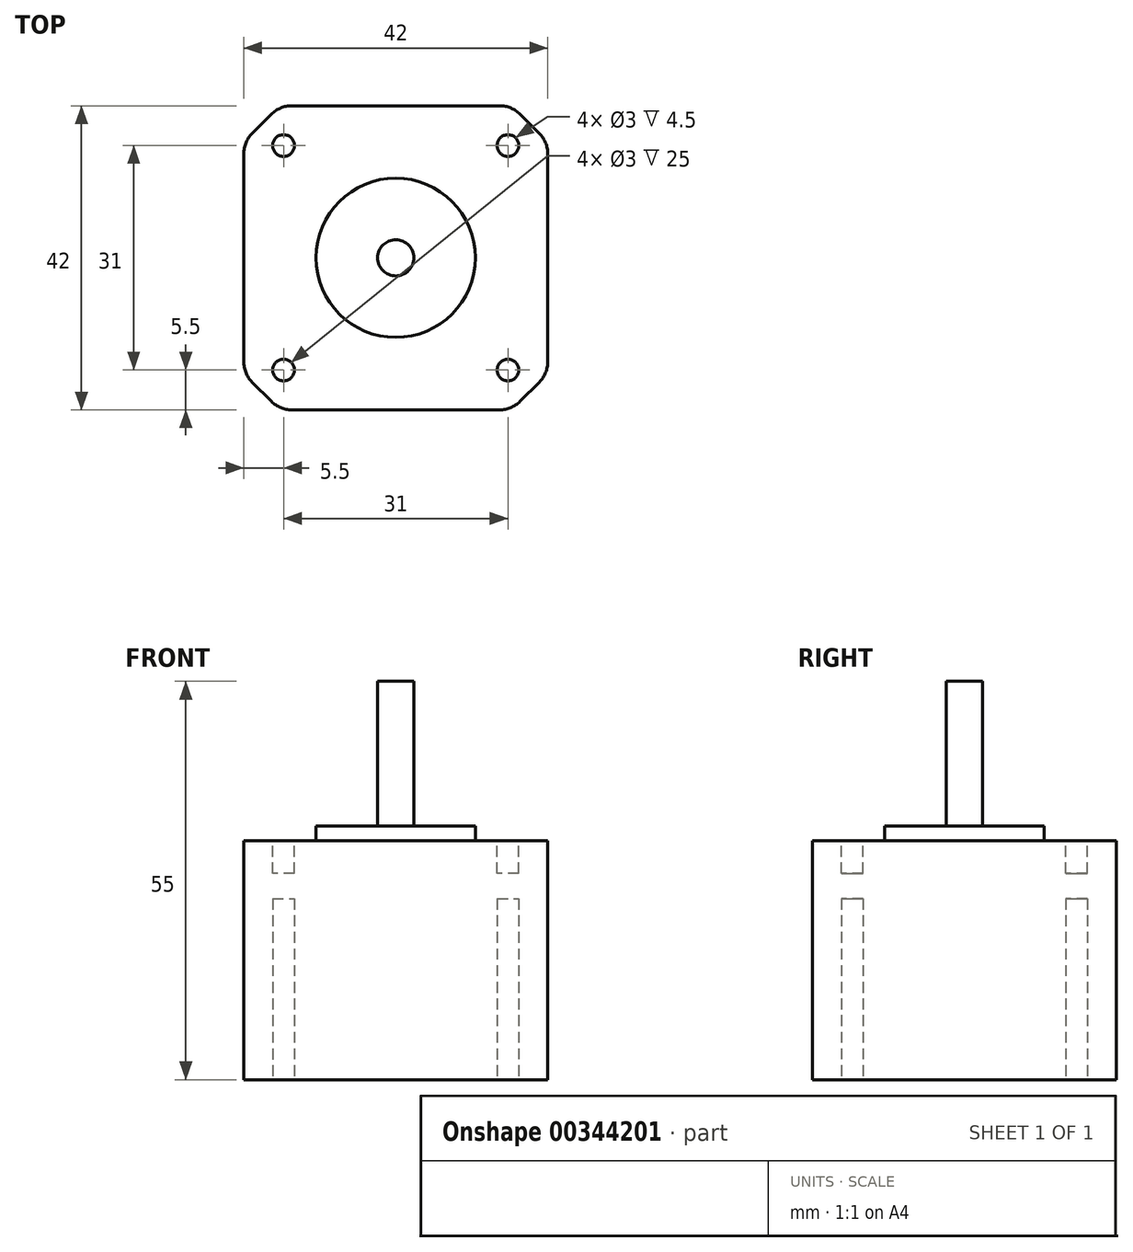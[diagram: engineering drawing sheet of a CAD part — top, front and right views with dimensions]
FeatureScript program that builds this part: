
annotation { "Feature Type Name" : "Feature", "Feature Type Description" : "" }
export const myFeature = defineFeature(function(context is Context, id is Id, definition is map)
    precondition{}
    {
        {
            var Q0;
            Q0=qCreatedBy(makeId("Top.planeOp"),FACE);
            var sketch = newSketch(context, id + "F0", { "sketchPlane" : qUnion([Q0])});
            skLineSegment(sketch, "E0.bottom", {"start": v(0, 0) * mm, "end": v(42, 0) * mm});
            skLineSegment(sketch, "E0.top", {"start": v(0, -42) * mm, "end": v(42, -42) * mm});
            skLineSegment(sketch, "E0.left", {"start": v(0, 0) * mm, "end": v(0, -42) * mm});
            skLineSegment(sketch, "E0.right", {"start": v(42, 0) * mm, "end": v(42, -42) * mm});
            skSolve(sketch);
        }
        {
            var Q0;
            Q0 = qSketchRegion(id + "F0", true);
            extrude(context, id + "F1", {"entities" : qUnion([Q0]), "depth" : 33 * mm});
        }
        {
            var Q0;
            Q0=makeQuery(id+"F1.opExtrude","CAP_FACE",FACE,{"disambiguationData":[OSD([sQuery(id+"F0.wireOp",EDGE,"E0.bottom"),sQuery(id+"F0.wireOp",EDGE,"E0.top"),sQuery(id+"F0.wireOp",EDGE,"E0.left"),sQuery(id+"F0.wireOp",EDGE,"E0.right")])],"isStart":false});
            var sketch = newSketch(context, id + "F2", { "sketchPlane" : qUnion([Q0])});
            skCircle(sketch, "E1", {"center": v(21, -21) * mm, "radius": 11 * mm});
            skPoint(sketch, "E1.centerSnap0", {"position": v(21, 0) * mm});
            skPoint(sketch, "E1.centerSnap1", {"position": v(42, -21) * mm});
            skSolve(sketch);
        }
        {
            var Q0;
            Q0 = qSketchRegion(id + "F2", true);
            extrude(context, id + "F3", {"entities" : qUnion([Q0]), "operationType" : NewBodyOperationType.ADD, "depth" : 2 * mm});
        }
        {
            var Q0;
            Q0=makeQuery(id+"F3.opExtrude","CAP_FACE",FACE,{"disambiguationData":[OSD([sQuery(id+"F2.wireOp",EDGE,"E1")])],"isStart":false});
            var sketch = newSketch(context, id + "F4", { "sketchPlane" : qUnion([Q0])});
            skCircle(sketch, "E2", {"center": v(21, -21) * mm, "radius": 2.5 * mm});
            skSolve(sketch);
        }
        {
            var Q0;
            Q0 = qSketchRegion(id + "F4", true);
            extrude(context, id + "F5", {"entities" : qUnion([Q0]), "operationType" : NewBodyOperationType.ADD, "depth" : 20 * mm});
        }
        {
            var Q0;
            Q0=makeQuery(id+"F1.opExtrude","CAP_FACE",FACE,{"disambiguationData":[OSD([sQuery(id+"F0.wireOp",EDGE,"E0.bottom"),sQuery(id+"F0.wireOp",EDGE,"E0.top"),sQuery(id+"F0.wireOp",EDGE,"E0.left"),sQuery(id+"F0.wireOp",EDGE,"E0.right")])],"isStart":false});
            var sketch = newSketch(context, id + "F6", { "sketchPlane" : qUnion([Q0])});
            skCircle(sketch, "E3", {"center": v(5.5, -5.5) * mm, "radius": 1.5 * mm});
            skCircle(sketch, "E4", {"center": v(36.5, -5.5) * mm, "radius": 1.5 * mm});
            skCircle(sketch, "E5", {"center": v(36.5, -36.5) * mm, "radius": 1.5 * mm});
            skCircle(sketch, "E6", {"center": v(5.5, -36.5) * mm, "radius": 1.5 * mm});
            skSolve(sketch);
        }
        {
            var Q0;
            Q0 = qSketchRegion(id + "F6", true);
            extrude(context, id + "F7", {"entities" : qUnion([Q0]), "operationType" : NewBodyOperationType.REMOVE, "oppositeDirection" : true, "depth" : 4.5 * mm});
        }
        {
            var Q0;
            Q0=makeQuery(id+"F1.opExtrude","SWEPT_EDGE",EDGE,{"disambiguationData":[OSD([sQuery(id+"F0.wireOp",EDGE,"E0.bottom"),sQuery(id+"F0.wireOp",EDGE,"E0.right")])]});
            var Q1;
            Q1=makeQuery(id+"F1.opExtrude","SWEPT_EDGE",EDGE,{"disambiguationData":[OSD([sQuery(id+"F0.wireOp",EDGE,"E0.top"),sQuery(id+"F0.wireOp",EDGE,"E0.right")])]});
            var Q2;
            Q2=makeQuery(id+"F1.opExtrude","SWEPT_EDGE",EDGE,{"disambiguationData":[OSD([sQuery(id+"F0.wireOp",EDGE,"E0.top"),sQuery(id+"F0.wireOp",EDGE,"E0.left")])]});
            var Q3;
            Q3=makeQuery(id+"F1.opExtrude","SWEPT_EDGE",EDGE,{"disambiguationData":[OSD([sQuery(id+"F0.wireOp",EDGE,"E0.bottom"),sQuery(id+"F0.wireOp",EDGE,"E0.left")])]});
            chamfer(context, id + "F8", {"entities" : qUnion([Q0, Q1, Q2, Q3]), "width" : 5 * mm, "tangentPropagation" : true});
        }
        {
            var Q0;
            {var subQ0=sQuery(id+"F0.wireOp",EDGE,"E0.left");Q0=makeQuery(id+"F8.opChamfer","BLEND_EDGE",EDGE,{"blendedFrom":[makeQuery(id+"F1.opExtrude","SWEPT_EDGE",EDGE,{"disambiguationData":[OSD([sQuery(id+"F0.wireOp",EDGE,"E0.bottom"),subQ0])]}),makeQuery(id+"F1.opExtrude","SWEPT_FACE",FACE,{"disambiguationData":[OSD([subQ0])]})],"blendedInto":[makeQuery(id+"F1.opExtrude","SWEPT_FACE",FACE,{"disambiguationData":[OSD([subQ0])]})]});}
            var Q1;
            {var subQ0=sQuery(id+"F0.wireOp",EDGE,"E0.bottom");Q1=makeQuery(id+"F8.opChamfer","BLEND_EDGE",EDGE,{"blendedFrom":[makeQuery(id+"F1.opExtrude","SWEPT_EDGE",EDGE,{"disambiguationData":[OSD([subQ0,sQuery(id+"F0.wireOp",EDGE,"E0.left")])]}),makeQuery(id+"F1.opExtrude","SWEPT_FACE",FACE,{"disambiguationData":[OSD([subQ0])]})],"blendedInto":[makeQuery(id+"F1.opExtrude","SWEPT_FACE",FACE,{"disambiguationData":[OSD([subQ0])]})]});}
            var Q2;
            {var subQ0=sQuery(id+"F0.wireOp",EDGE,"E0.left");Q2=makeQuery(id+"F8.opChamfer","BLEND_EDGE",EDGE,{"blendedFrom":[makeQuery(id+"F1.opExtrude","SWEPT_EDGE",EDGE,{"disambiguationData":[OSD([sQuery(id+"F0.wireOp",EDGE,"E0.top"),subQ0])]}),makeQuery(id+"F1.opExtrude","SWEPT_FACE",FACE,{"disambiguationData":[OSD([subQ0])]})],"blendedInto":[makeQuery(id+"F1.opExtrude","SWEPT_FACE",FACE,{"disambiguationData":[OSD([subQ0])]})]});}
            var Q3;
            {var subQ0=sQuery(id+"F0.wireOp",EDGE,"E0.top");Q3=makeQuery(id+"F8.opChamfer","BLEND_EDGE",EDGE,{"blendedFrom":[makeQuery(id+"F1.opExtrude","SWEPT_EDGE",EDGE,{"disambiguationData":[OSD([subQ0,sQuery(id+"F0.wireOp",EDGE,"E0.left")])]}),makeQuery(id+"F1.opExtrude","SWEPT_FACE",FACE,{"disambiguationData":[OSD([subQ0])]})],"blendedInto":[makeQuery(id+"F1.opExtrude","SWEPT_FACE",FACE,{"disambiguationData":[OSD([subQ0])]})]});}
            var Q4;
            {var subQ0=sQuery(id+"F0.wireOp",EDGE,"E0.top");Q4=makeQuery(id+"F8.opChamfer","BLEND_EDGE",EDGE,{"blendedFrom":[makeQuery(id+"F1.opExtrude","SWEPT_EDGE",EDGE,{"disambiguationData":[OSD([subQ0,sQuery(id+"F0.wireOp",EDGE,"E0.right")])]}),makeQuery(id+"F1.opExtrude","SWEPT_FACE",FACE,{"disambiguationData":[OSD([subQ0])]})],"blendedInto":[makeQuery(id+"F1.opExtrude","SWEPT_FACE",FACE,{"disambiguationData":[OSD([subQ0])]})]});}
            var Q5;
            {var subQ0=sQuery(id+"F0.wireOp",EDGE,"E0.right");Q5=makeQuery(id+"F8.opChamfer","BLEND_EDGE",EDGE,{"blendedFrom":[makeQuery(id+"F1.opExtrude","SWEPT_EDGE",EDGE,{"disambiguationData":[OSD([sQuery(id+"F0.wireOp",EDGE,"E0.top"),subQ0])]}),makeQuery(id+"F1.opExtrude","SWEPT_FACE",FACE,{"disambiguationData":[OSD([subQ0])]})],"blendedInto":[makeQuery(id+"F1.opExtrude","SWEPT_FACE",FACE,{"disambiguationData":[OSD([subQ0])]})]});}
            var Q6;
            {var subQ0=sQuery(id+"F0.wireOp",EDGE,"E0.bottom");Q6=makeQuery(id+"F8.opChamfer","BLEND_EDGE",EDGE,{"blendedFrom":[makeQuery(id+"F1.opExtrude","SWEPT_EDGE",EDGE,{"disambiguationData":[OSD([subQ0,sQuery(id+"F0.wireOp",EDGE,"E0.right")])]}),makeQuery(id+"F1.opExtrude","SWEPT_FACE",FACE,{"disambiguationData":[OSD([subQ0])]})],"blendedInto":[makeQuery(id+"F1.opExtrude","SWEPT_FACE",FACE,{"disambiguationData":[OSD([subQ0])]})]});}
            var Q7;
            {var subQ0=sQuery(id+"F0.wireOp",EDGE,"E0.right");Q7=makeQuery(id+"F8.opChamfer","BLEND_EDGE",EDGE,{"blendedFrom":[makeQuery(id+"F1.opExtrude","SWEPT_EDGE",EDGE,{"disambiguationData":[OSD([sQuery(id+"F0.wireOp",EDGE,"E0.bottom"),subQ0])]}),makeQuery(id+"F1.opExtrude","SWEPT_FACE",FACE,{"disambiguationData":[OSD([subQ0])]})],"blendedInto":[makeQuery(id+"F1.opExtrude","SWEPT_FACE",FACE,{"disambiguationData":[OSD([subQ0])]})]});}
            fillet(context, id + "F9", {"entities" : qUnion([Q0, Q1, Q2, Q3, Q4, Q5, Q6, Q7]), "radius" : 4 * mm, "tangentPropagation" : true, "allowEdgeOverflow" : false});
        }
        {
            var Q0;
            Q0=makeQuery(id+"F1.opExtrude","CAP_FACE",FACE,{"disambiguationData":[OSD([sQuery(id+"F0.wireOp",EDGE,"E0.bottom"),sQuery(id+"F0.wireOp",EDGE,"E0.top"),sQuery(id+"F0.wireOp",EDGE,"E0.left"),sQuery(id+"F0.wireOp",EDGE,"E0.right")])],"isStart":true});
            var sketch = newSketch(context, id + "F10", { "sketchPlane" : qUnion([Q0])});
            skPoint(sketch, "E7.firstSnap0", {"position": v(21, 42) * mm});
            skPoint(sketch, "E7.firstSnap1", {"position": v(42, 21) * mm});
            skCircle(sketch, "E8", {"center": v(36.5, 36.5) * mm, "radius": 1.5 * mm});
            skCircle(sketch, "E9", {"center": v(5.5, 36.5) * mm, "radius": 1.5 * mm});
            skCircle(sketch, "E10", {"center": v(5.5, 5.5) * mm, "radius": 1.5 * mm});
            skCircle(sketch, "E11", {"center": v(36.5, 5.5) * mm, "radius": 1.5 * mm});
            skSolve(sketch);
        }
        {
            var Q0;
            Q0 = qSketchRegion(id + "F10", true);
            extrude(context, id + "F11", {"entities" : qUnion([Q0]), "operationType" : NewBodyOperationType.REMOVE, "oppositeDirection" : true, "depth" : 25 * mm});
        }
    });
